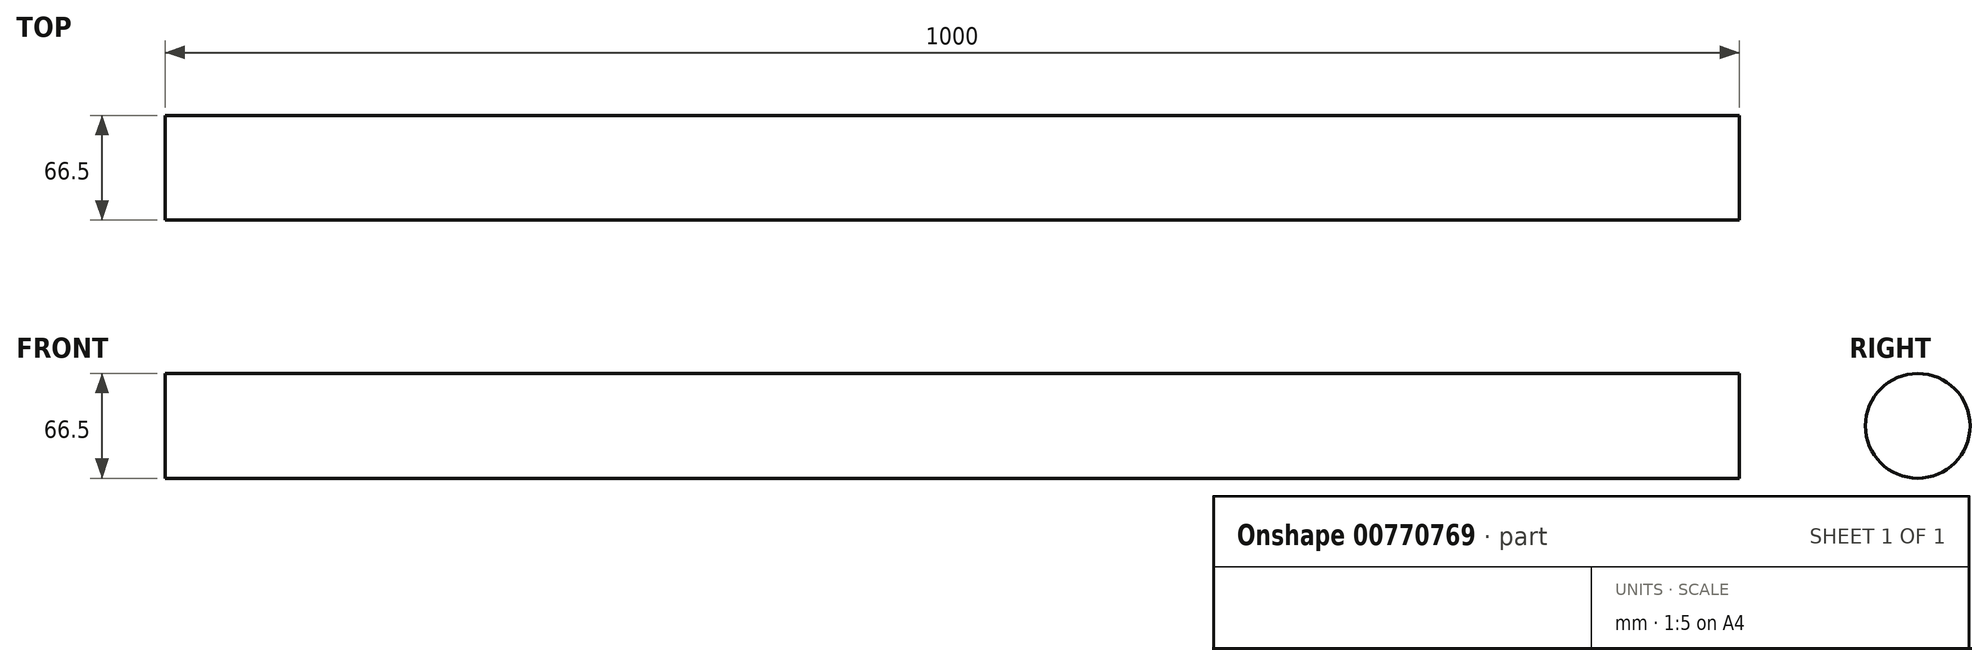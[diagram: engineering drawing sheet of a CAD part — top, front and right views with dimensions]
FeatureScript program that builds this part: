
annotation { "Feature Type Name" : "Feature", "Feature Type Description" : "" }
export const myFeature = defineFeature(function(context is Context, id is Id, definition is map)
    precondition{}
    {
        {
            var Q0;
            Q0=qCreatedBy(makeId("Right.planeOp"),FACE);
            var sketch = newSketch(context, id + "F0", { "sketchPlane" : qUnion([Q0])});
            skCircle(sketch, "E0", {"center": v(0, 0) * mm, "radius": 33.25 * mm});
            skSolve(sketch);
        }
        {
            var Q0;
            Q0 = qSketchRegion(id + "F0", true);
            extrude(context, id + "F1", {"entities" : qUnion([Q0]), "depth" : 1000 * mm, "offsetDistance" : 25 * mm});
        }
    });
